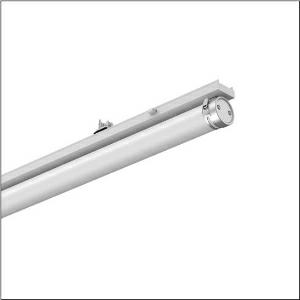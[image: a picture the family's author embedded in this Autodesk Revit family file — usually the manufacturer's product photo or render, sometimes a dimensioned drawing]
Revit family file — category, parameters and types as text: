
# Revit family: monsun_r__31_tube_51ft10nn4a0atr2_f2a8
name_source: partatom
category: Lighting Fixtures
units: mm (PartAtom-declared; Revit-internal decimal feet)

## family parameters
Cut with Voids When Loaded = No
Host = Face
Light Source = No
Part Type = Normal
Room Calculation Point = No
Round Connector Dimension = Use Diameter
Shared = No

## types (1)
- --- (1 x LED, 10000 lm, 58 W, 4000K)
    Apparent Load = 58 VA
    CIE Flux Codes = 42 71 90 91 100
    Color Rendering = 80
    Color Temperature = 4000K
    Default Elevation = 1800 mm
    Description = Monsun® 31 Tube, tubular luminaire, primary optical cover: diffuser, of PMMA, light emission: direct distribution, primary light characteristic: symmetric, LED, rated luminous flux: 10.000lm, luminous efficacy: 172lm/W, light colour: 840, colour temperature: 4000K, control gear: DALI Multilumen, with with 1 terminal, 5-pole, max. 2.5mm², mains connection: 220..240V, AC, 50/60Hz, rated input power: 58W, housing, cylindrical, of PMMA, semi-transparent, matt white, with luminaire and ceiling fastening, V4A, mounting with brackets of stainless steel, length: 1.500mm, diameter: 75mm, end cap, of stainless steel (V4A), protection rating (complete): IP20, protection rating (lamp compartment): IP67/69K, insulation class (complete): insulation class I (protective earthing), certification: CE, UKCA, impact resistance: IK06, permissible operating ambient temperature: -20..+40°C, corresponds to IFS (International Featured Standards) requirements for safety and quality in the food industry, contact your sales advisor before using the luminaires in applications with unclear chemical exposure, large temperature fluctuations or condensation-forming humidity, packaging unit: 1 piece
    Height = 132 mm
    Lamp = 1 x LED
    Lamp Light Flux = 10000 lm
    Lamp Power = 58 W
    Lamp count = 1
    Length = 1500 mm
    Luminous efficacy = 172 lm/W
    Manufacturer = Siteco
    ModVariant = No
    Model = 51FT10NN4A0ATR2
    Mounting Place = Ceiling
    Mounting Type = Pendant
    Number of Poles = 1
    OnlyDefault = Yes
    Power Factor = 1
    Product Name = Monsun® 31 Tube
    Product group = tubular luminaire
    ProductGroupID = 907
    Protection Class = Protection class I
    Protection Degree = IP 20
    RLX_Detail_Level = 1
    RLX_Emergency_Light_Flux = 0 lm
    RLX_Emergency_Type = 0
    RLX_Emergency_Type_DB = No
    RlxData = <blob elided: 32473 chars, md5=ad936c34>
    Socket = socket
    Standby Power = 0 W
    System Light Flux = 10000 lm
    System Power = 58 W
    Type Comments = individual setting: luminous flux: 100 % | (OFF | OFF | ON | OFF) | 350 mA
    Type Image = l_1242814.jpg
    URL = http://relux.com
    VarID = @adj_143354
    Voltage = 0 V
    Weight = 0.00 kg
    Width = 79 mm

## geometry (parser evidence)
native form markers: Blend x4, Sweep x10
no freeform markers — native parametric forms only
